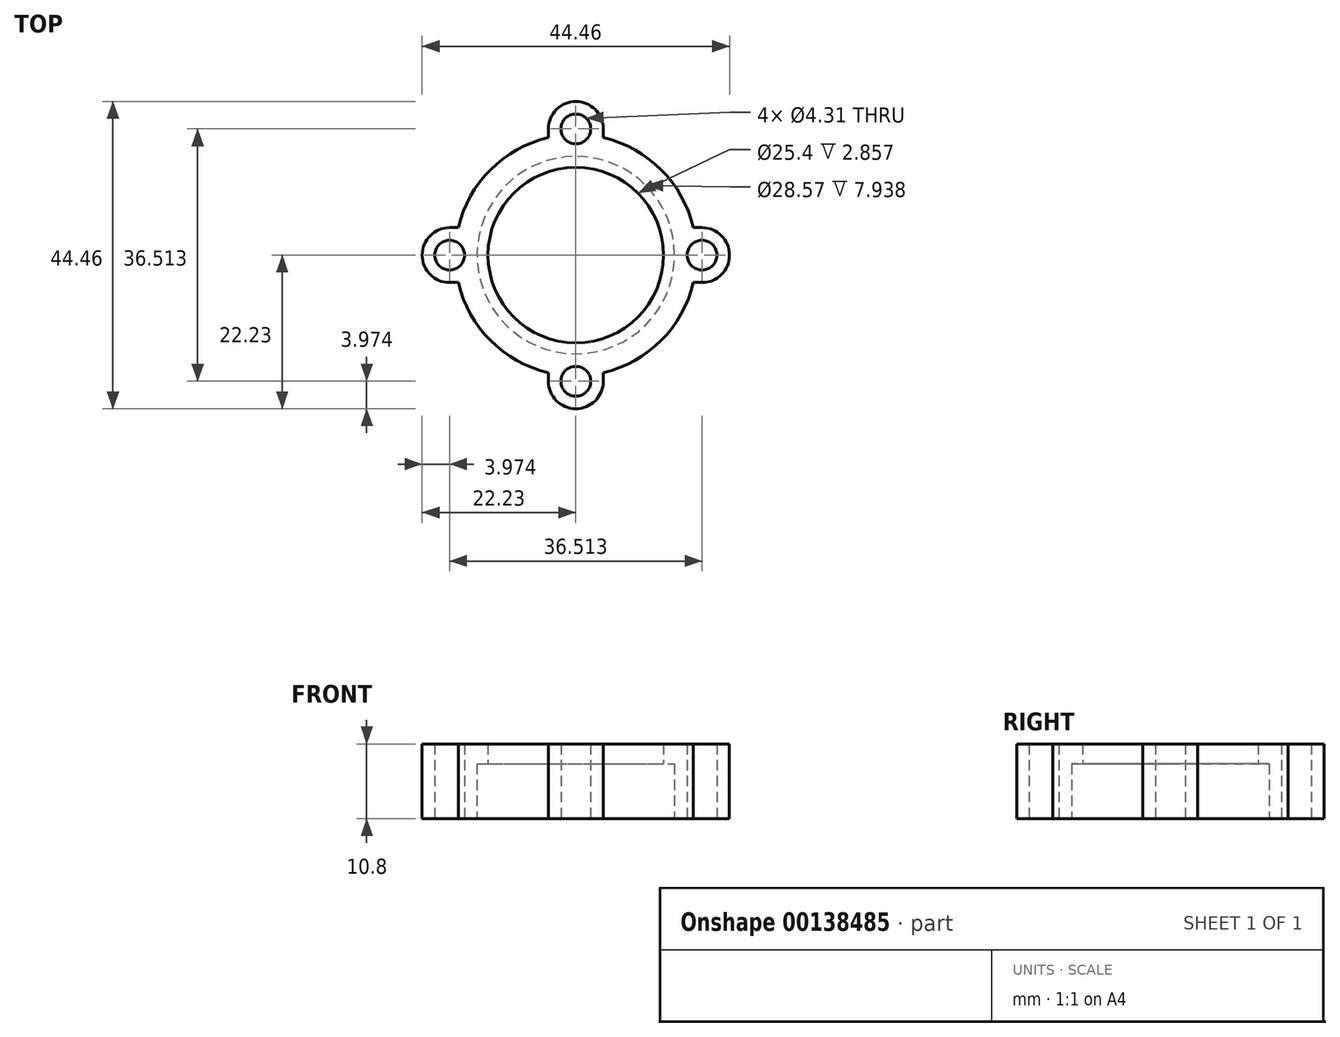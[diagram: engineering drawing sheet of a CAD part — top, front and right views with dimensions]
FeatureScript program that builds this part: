
annotation { "Feature Type Name" : "Feature", "Feature Type Description" : "" }
export const myFeature = defineFeature(function(context is Context, id is Id, definition is map)
    precondition{}
    {
        {
            var Q0;
            Q0=qCreatedBy(makeId("Top.planeOp"),FACE);
            var sketch = newSketch(context, id + "F0", { "sketchPlane" : qUnion([Q0])});
            skCircle(sketch, "E0", {"center": v(0, 0) * mm, "radius": 12.7 * mm});
            skCircle(sketch, "E1", {"center": v(-18.26, 0) * mm, "radius": 2.15 * mm});
            skCircle(sketch, "E2", {"center": v(0, 18.26) * mm, "radius": 2.15 * mm});
            skCircle(sketch, "E3", {"center": v(18.26, 0) * mm, "radius": 2.15 * mm});
            skCircle(sketch, "E4", {"center": v(0, -18.26) * mm, "radius": 2.15 * mm});
            skLineSegment(sketch, "E5", {"start": v(-18.26, 0) * mm, "end": v(0, 0) * mm, "construction": true});
            skLineSegment(sketch, "E6", {"start": v(0, 0) * mm, "end": v(18.26, 0) * mm, "construction": true});
            skLineSegment(sketch, "E7", {"start": v(0, 18.26) * mm, "end": v(0, 0) * mm, "construction": true});
            skLineSegment(sketch, "E8", {"start": v(0, 0) * mm, "end": v(0, -18.26) * mm, "construction": true});
            skLineSegment(sketch, "E9.bottom", {"start": v(-18.26, 3.97) * mm, "end": v(-17, 3.97) * mm});
            skLineSegment(sketch, "E9.top", {"start": v(-18.26, -3.97) * mm, "end": v(-17, -3.97) * mm});
            skLineSegment(sketch, "E9.left", {"start": v(-18.26, 3.97) * mm, "end": v(-18.26, -3.97) * mm, "construction": true});
            skLineSegment(sketch, "E9.right", {"start": v(-17, 3.97) * mm, "end": v(-17, -3.97) * mm, "construction": true});
            skLineSegment(sketch, "E10.bottom", {"start": v(3.97, 18.26) * mm, "end": v(-3.97, 18.26) * mm, "construction": true});
            skLineSegment(sketch, "E10.top", {"start": v(3.97, 17) * mm, "end": v(-3.97, 17) * mm, "construction": true});
            skLineSegment(sketch, "E10.left", {"start": v(3.97, 18.26) * mm, "end": v(3.97, 17) * mm});
            skLineSegment(sketch, "E10.right", {"start": v(-3.97, 18.26) * mm, "end": v(-3.97, 17) * mm});
            skLineSegment(sketch, "E11.bottom", {"start": v(18.26, -3.97) * mm, "end": v(17, -3.97) * mm});
            skLineSegment(sketch, "E11.top", {"start": v(18.26, 3.97) * mm, "end": v(17, 3.97) * mm});
            skLineSegment(sketch, "E11.left", {"start": v(18.26, -3.97) * mm, "end": v(18.26, 3.97) * mm, "construction": true});
            skLineSegment(sketch, "E11.right", {"start": v(17, -3.97) * mm, "end": v(17, 3.97) * mm, "construction": true});
            skLineSegment(sketch, "E12.bottom", {"start": v(3.97, -17) * mm, "end": v(-3.97, -17) * mm, "construction": true});
            skLineSegment(sketch, "E12.top", {"start": v(3.97, -18.26) * mm, "end": v(-3.97, -18.26) * mm, "construction": true});
            skLineSegment(sketch, "E12.left", {"start": v(3.97, -18.26) * mm, "end": v(3.97, -17) * mm});
            skLineSegment(sketch, "E12.right", {"start": v(-3.97, -18.26) * mm, "end": v(-3.97, -17) * mm});
            skArc(sketch, "E13", {"start": v(-17, -3.97) * mm, "mid": v(-12.35, -12.35) * mm, "end": v(-3.97, -17) * mm});
            skArc(sketch, "E14", {"start": v(-3.97, 17) * mm, "mid": v(-12.35, 12.35) * mm, "end": v(-17, 3.97) * mm});
            skArc(sketch, "E15", {"start": v(3.97, -17) * mm, "mid": v(12.35, -12.35) * mm, "end": v(17, -3.97) * mm});
            skArc(sketch, "E16", {"start": v(17, 3.97) * mm, "mid": v(12.35, 12.35) * mm, "end": v(3.97, 17) * mm});
            skArc(sketch, "E17", {"start": v(3.97, 18.26) * mm, "mid": v(0, 22.22) * mm, "end": v(-3.97, 18.26) * mm});
            skArc(sketch, "E18", {"start": v(18.26, -3.97) * mm, "mid": v(22.22, 0) * mm, "end": v(18.26, 3.97) * mm});
            skArc(sketch, "E19", {"start": v(-3.97, -18.26) * mm, "mid": v(0, -22.23) * mm, "end": v(3.97, -18.26) * mm});
            skArc(sketch, "E20", {"start": v(-18.26, 3.97) * mm, "mid": v(-22.23, 0) * mm, "end": v(-18.26, -3.97) * mm});
            skSolve(sketch);
        }
        {
            var Q0;
            Q0 = qSketchRegion(id + "F0", true);
            extrude(context, id + "F1", {"entities" : qUnion([Q0]), "depth" : 10.8 * mm});
        }
        {
            var Q0;
            Q0=makeQuery(id+"F1.opExtrude","CAP_FACE",FACE,{"disambiguationData":[OSD([sQuery(id+"F0.wireOp",EDGE,"E0"),sQuery(id+"F0.wireOp",EDGE,"E1"),sQuery(id+"F0.wireOp",EDGE,"E2"),sQuery(id+"F0.wireOp",EDGE,"E3"),sQuery(id+"F0.wireOp",EDGE,"E4"),sQuery(id+"F0.wireOp",EDGE,"E9.bottom"),sQuery(id+"F0.wireOp",EDGE,"E9.top"),sQuery(id+"F0.wireOp",EDGE,"E10.left"),sQuery(id+"F0.wireOp",EDGE,"E10.right"),sQuery(id+"F0.wireOp",EDGE,"E11.bottom"),sQuery(id+"F0.wireOp",EDGE,"E11.top"),sQuery(id+"F0.wireOp",EDGE,"E12.left"),sQuery(id+"F0.wireOp",EDGE,"E12.right"),sQuery(id+"F0.wireOp",EDGE,"E13"),sQuery(id+"F0.wireOp",EDGE,"E14"),sQuery(id+"F0.wireOp",EDGE,"E15"),sQuery(id+"F0.wireOp",EDGE,"E16"),sQuery(id+"F0.wireOp",EDGE,"E17"),sQuery(id+"F0.wireOp",EDGE,"E18"),sQuery(id+"F0.wireOp",EDGE,"E19"),sQuery(id+"F0.wireOp",EDGE,"E20")])],"isStart":true});
            var sketch = newSketch(context, id + "F2", { "sketchPlane" : qUnion([Q0])});
            skCircle(sketch, "E21", {"center": v(0, 0) * mm, "radius": 14.29 * mm});
            skSolve(sketch);
        }
        {
            var Q0;
            Q0 = qSketchRegion(id + "F2", true);
            extrude(context, id + "F3", {"entities" : qUnion([Q0]), "operationType" : NewBodyOperationType.REMOVE, "oppositeDirection" : true, "depth" : 7.94 * mm});
        }
    });
